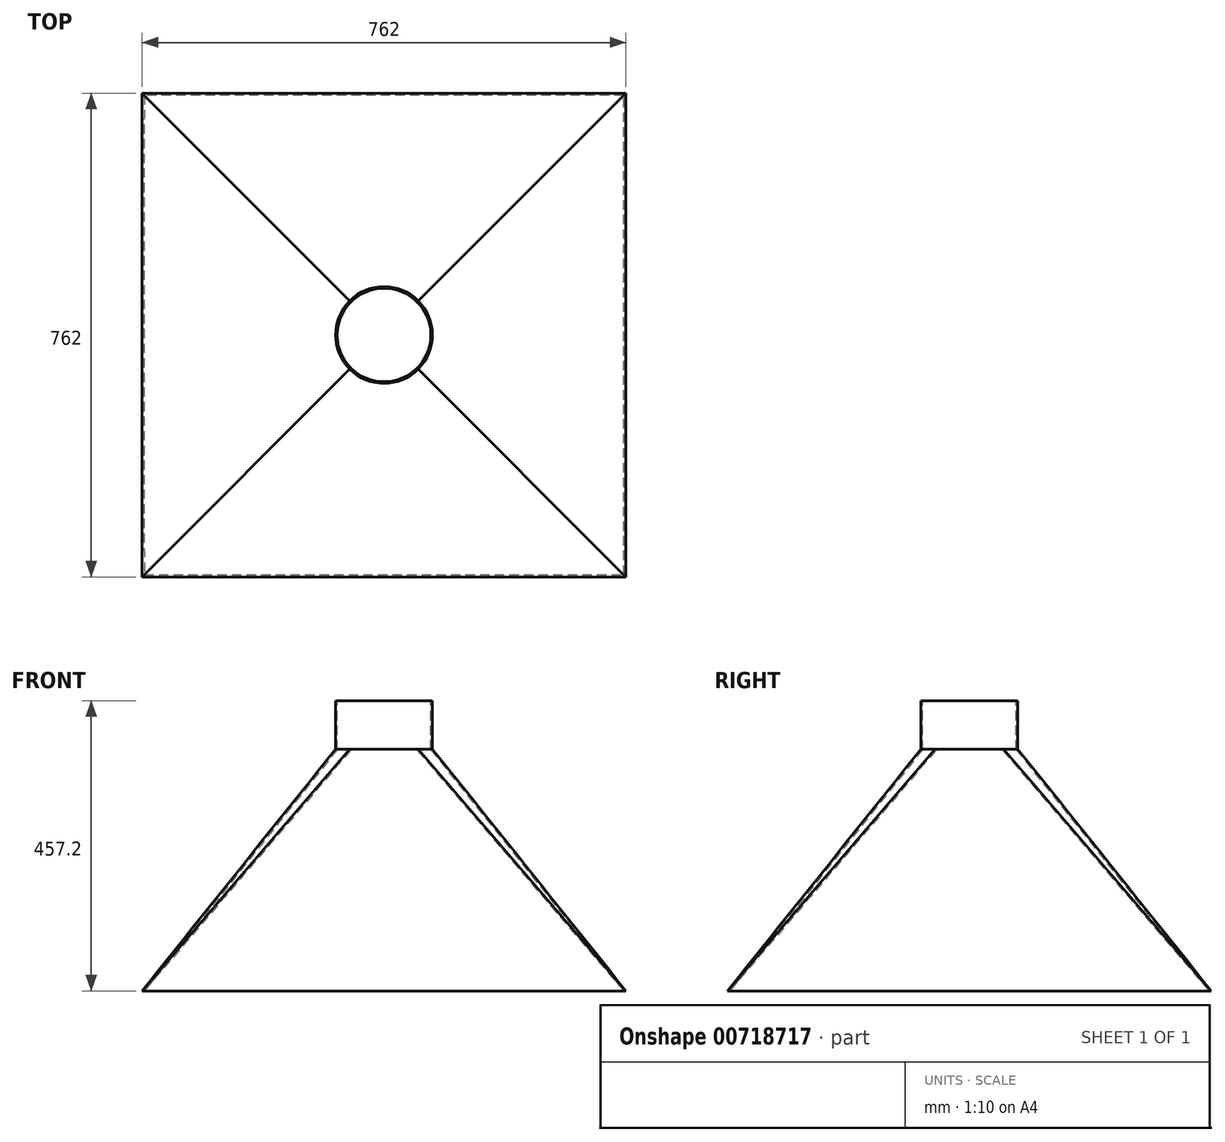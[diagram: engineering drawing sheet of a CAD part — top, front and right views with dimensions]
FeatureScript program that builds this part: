
annotation { "Feature Type Name" : "Feature", "Feature Type Description" : "" }
export const myFeature = defineFeature(function(context is Context, id is Id, definition is map)
    precondition{}
    {
        {
            var Q0;
            Q0=qCreatedBy(makeId("Top.planeOp"),FACE);
            var sketch = newSketch(context, id + "F0", { "sketchPlane" : qUnion([Q0])});
            skLineSegment(sketch, "E0.bottom", {"start": v(0, 0) * mm, "end": v(762, 0) * mm});
            skLineSegment(sketch, "E0.top", {"start": v(0, 762) * mm, "end": v(762, 762) * mm});
            skLineSegment(sketch, "E0.left", {"start": v(0, 0) * mm, "end": v(0, 762) * mm});
            skLineSegment(sketch, "E0.right", {"start": v(762, 0) * mm, "end": v(762, 762) * mm});
            skSolve(sketch);
        }
        {
            var Q0;
            Q0=qCreatedBy(makeId("Top.planeOp"),FACE);
            cPlane(context, id + "F1", {"entities" : qUnion([Q0]), "cplaneType" : CPlaneType.OFFSET, "offset" : 381 * mm, "width" : 152.4 * mm, "height" : 152.4 * mm});
        }
        {
            var Q0;
            Q0=qCreatedBy(id+"F1.planeOp",FACE);
            var sketch = newSketch(context, id + "F2", { "sketchPlane" : qUnion([Q0])});
            skCircle(sketch, "E1", {"center": v(381, 381) * mm, "radius": 76.2 * mm});
            skSolve(sketch);
        }
        {
            var Q0;
            Q0=makeQuery(id+"F0.imprint","IMPRINT",FACE,{"disambiguationData":[TD([[makeQuery(id+"F0.imprint","IMPRINT",EDGE,{"derivedFrom":sQuery(id+"F0.wireOp",EDGE,"E0.bottom")}),1.0]])]});
            var Q1;
            Q1=makeQuery(id+"F2.imprint","IMPRINT",FACE,{"disambiguationData":[TD([[makeQuery(id+"F2.imprint","IMPRINT",EDGE,{"derivedFrom":sQuery(id+"F2.wireOp",EDGE,"E1")}),1.0]])]});
            loft(context, id + "F3", {"sheetProfilesArray" : [{ "sheetProfileEntities" : qUnion([Q0]) }, { "sheetProfileEntities" : qUnion([Q1]) }]});
        }
        {
            var Q0;
            Q0=makeQuery(id+"F3.opLoft","CAP_FACE",FACE,{"disambiguationData":[OSD([makeQuery(id+"F2.imprint","IMPRINT",FACE,{"disambiguationData":[TD([[makeQuery(id+"F2.imprint","IMPRINT",EDGE,{"derivedFrom":sQuery(id+"F2.wireOp",EDGE,"E1")}),1.0]])]})])],"isStart":true});
            extrude(context, id + "F4", {"entities" : qUnion([Q0]), "operationType" : NewBodyOperationType.ADD, "depth" : 76.2 * mm});
        }
        {
            var Q0;
            Q0=makeQuery(id+"F3.opLoft","CAP_FACE",FACE,{"disambiguationData":[OSD([makeQuery(id+"F0.imprint","IMPRINT",FACE,{"disambiguationData":[TD([[makeQuery(id+"F0.imprint","IMPRINT",EDGE,{"derivedFrom":sQuery(id+"F0.wireOp",EDGE,"E0.bottom")}),1.0]])]})])],"isStart":true});
            var Q1;
            Q1=makeQuery(id+"F4.opExtrude","CAP_FACE",FACE,{"disambiguationData":[OSD([makeQuery(id+"F2.imprint","IMPRINT",FACE,{"disambiguationData":[TD([[makeQuery(id+"F2.imprint","IMPRINT",EDGE,{"derivedFrom":sQuery(id+"F2.wireOp",EDGE,"E1")}),1.0]])]})])],"isStart":false});
            shell(context, id + "F5", {"entities" : qUnion([Q0, Q1]), "thickness" : 2.54 * mm});
        }
    });
